# Revit family: SAE102-W
name_source: partatom
category: Lighting Fixtures
units: mm (PartAtom-declared; Revit-internal decimal feet)

## family parameters
Cut with Voids When Loaded = No
Host = Face
Light Source = Yes
OmniClass Number = 23.80.70.11.14.17
OmniClass Title = Direct/Indirect
Part Type = Normal
Room Calculation Point = No
Round Connector Dimension = Use Diameter
Shared = Yes

## types (5) — shared parameters
Apparent Load = 0 VA
Assembly Code = D5020200
Circuiting = 1 Circuit/2 Circuit - Uplight/Downlight
Color Filter = 16777215
Default Elevation = 4' - 0"
Description = Linear Pendant Indirect/Direct
Dimming Lamp Color Temperature Shift = <None>
Downlight Diffuser = Soft Glow Lens
Emit Shape Visible in Rendering = No
Emit from Rectangle Width = 0' - 4"
Fixture Distribution = Indirect/Direct
Glass = White Glass
Housing Material = Paint - Matte White
Lamp = LED's
Load Classification = Lighting
Manufacturer = Litecontrol
Model = SAE102-W
Mounting = Wall Mount
Photometric Notes = More IES files download on Photometric Web Link
Photometric Web File = SAE102-W-ID-STD-4-SOF-CX-35K-I050-D040.ies
Power Factor = 1
Tilt Angle = -90.00°
Type Comments = Lighting FIxture
URL = https://www.currentlighting.com
Voltage = 120 V
Warranty = 5-Years Warranty
Wattage Comments = 133 lumens/watt

## per-type parameters (varying)
| type | Emit from Rectangle Length | Row Length | zz Length 1 | zz YesNo 1 |
| SAE102-W-04 | 3' - 10" | 4' - 0" | 1' - 0" | No |
| SAE102-W-02 | 1' - 10" | 2' - 0" | 0' - 0" | Yes |
| SAE102-W-03 | 2' - 10" | 3' - 0" | 0' - 6" | No |
| SAE102-W-06 | 5' - 10" | 6' - 0" | 1' - 0" | No |
| SAE102-W-08 | 7' - 10" | 8' - 0" | 1' - 0" | No |

## geometry (parser evidence)
native form markers: Sweep x6
no freeform markers — native parametric forms only
